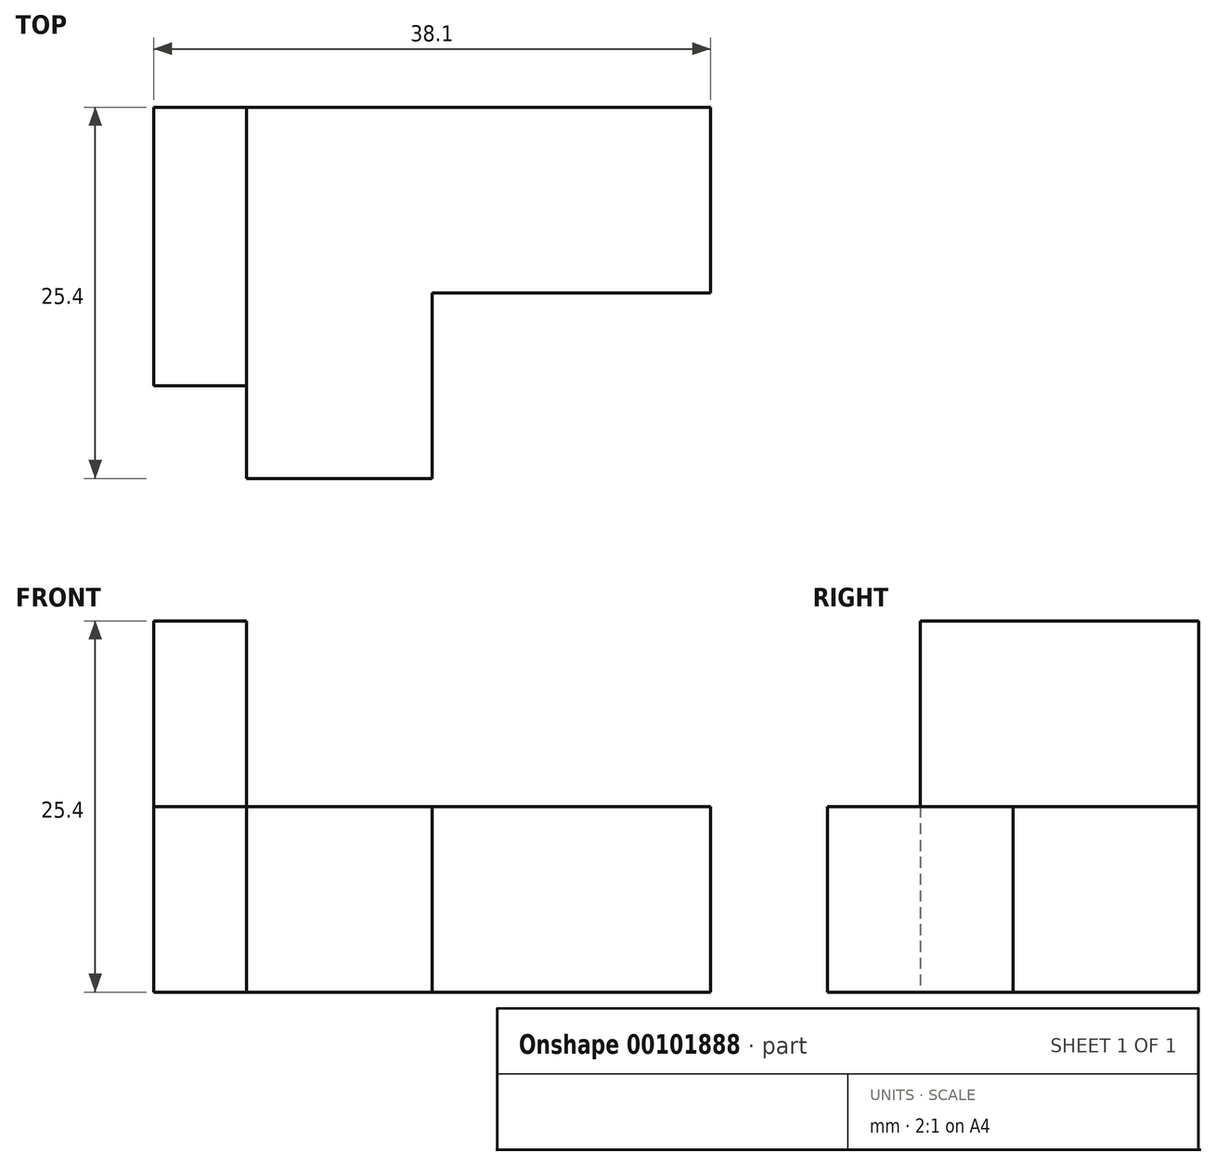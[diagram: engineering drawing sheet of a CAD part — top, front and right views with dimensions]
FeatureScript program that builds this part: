
annotation { "Feature Type Name" : "Feature", "Feature Type Description" : "" }
export const myFeature = defineFeature(function(context is Context, id is Id, definition is map)
    precondition{}
    {
        {
            var Q0;
            Q0=qCreatedBy(makeId("Front.planeOp"),FACE);
            var sketch = newSketch(context, id + "F0", { "sketchPlane" : qUnion([Q0])});
            skLineSegment(sketch, "E0", {"start": v(0, 0) * mm, "end": v(0, 12.7) * mm});
            skLineSegment(sketch, "E1", {"start": v(0, 12.7) * mm, "end": v(38.1, 12.7) * mm});
            skLineSegment(sketch, "E2", {"start": v(38.1, 12.7) * mm, "end": v(38.1, 0) * mm});
            skLineSegment(sketch, "E3", {"start": v(38.1, 0) * mm, "end": v(0, 0) * mm});
            skSolve(sketch);
        }
        {
            var Q0;
            Q0 = qSketchRegion(id + "F0", true);
            extrude(context, id + "F1", {"entities" : qUnion([Q0]), "endBound" : BoundingType.SYMMETRIC, "depth" : 25.4 * mm});
        }
        {
            var Q0;
            Q0=qCreatedBy(makeId("Top.planeOp"),FACE);
            var sketch = newSketch(context, id + "F2", { "sketchPlane" : qUnion([Q0])});
            skLineSegment(sketch, "E4.bottom", {"start": v(38.1, -12.7) * mm, "end": v(19.05, -12.7) * mm});
            skLineSegment(sketch, "E4.top", {"start": v(38.1, 0) * mm, "end": v(19.05, 0) * mm});
            skLineSegment(sketch, "E4.left", {"start": v(38.1, -12.7) * mm, "end": v(38.1, 0) * mm});
            skLineSegment(sketch, "E4.right", {"start": v(19.05, -12.7) * mm, "end": v(19.05, 0) * mm});
            skSolve(sketch);
        }
        {
            var Q0;
            Q0 = qSketchRegion(id + "F2", true);
            extrude(context, id + "F3", {"entities" : qUnion([Q0]), "operationType" : NewBodyOperationType.REMOVE, "endBound" : BoundingType.THROUGH_ALL, "depth" : 25.4 * mm});
        }
        {
            var Q0;
            Q0=qCreatedBy(makeId("Front.planeOp"),FACE);
            var sketch = newSketch(context, id + "F4", { "sketchPlane" : qUnion([Q0])});
            skLineSegment(sketch, "E5.bottom", {"start": v(0, 12.7) * mm, "end": v(6.35, 12.7) * mm});
            skLineSegment(sketch, "E5.top", {"start": v(0, 25.4) * mm, "end": v(6.35, 25.4) * mm});
            skLineSegment(sketch, "E5.left", {"start": v(0, 12.7) * mm, "end": v(0, 25.4) * mm});
            skLineSegment(sketch, "E5.right", {"start": v(6.35, 12.7) * mm, "end": v(6.35, 25.4) * mm});
            skSolve(sketch);
        }
        {
            var Q0;
            Q0=makeQuery(id+"F4.imprint","IMPRINT",FACE,{"disambiguationData":[TD([[makeQuery(id+"F4.imprint","IMPRINT",EDGE,{"derivedFrom":sQuery(id+"F4.wireOp",EDGE,"E5.bottom")}),1.0]])]});
            extrude(context, id + "F5", {"entities" : qUnion([Q0]), "endBound" : BoundingType.SYMMETRIC, "depth" : 25.4 * mm});
        }
        {
            var Q0;
            Q0=qCreatedBy(makeId("Top.planeOp"),FACE);
            var sketch = newSketch(context, id + "F6", { "sketchPlane" : qUnion([Q0])});
            skLineSegment(sketch, "E6.bottom", {"start": v(0, -12.7) * mm, "end": v(6.35, -12.7) * mm});
            skLineSegment(sketch, "E6.top", {"start": v(0, -6.35) * mm, "end": v(6.35, -6.35) * mm});
            skLineSegment(sketch, "E6.left", {"start": v(0, -12.7) * mm, "end": v(0, -6.35) * mm});
            skLineSegment(sketch, "E6.right", {"start": v(6.35, -12.7) * mm, "end": v(6.35, -6.35) * mm});
            skSolve(sketch);
        }
        {
            var Q0;
            Q0 = qSketchRegion(id + "F6", true);
            extrude(context, id + "F7", {"entities" : qUnion([Q0]), "operationType" : NewBodyOperationType.REMOVE, "endBound" : BoundingType.THROUGH_ALL, "depth" : 25.4 * mm});
        }
    });
